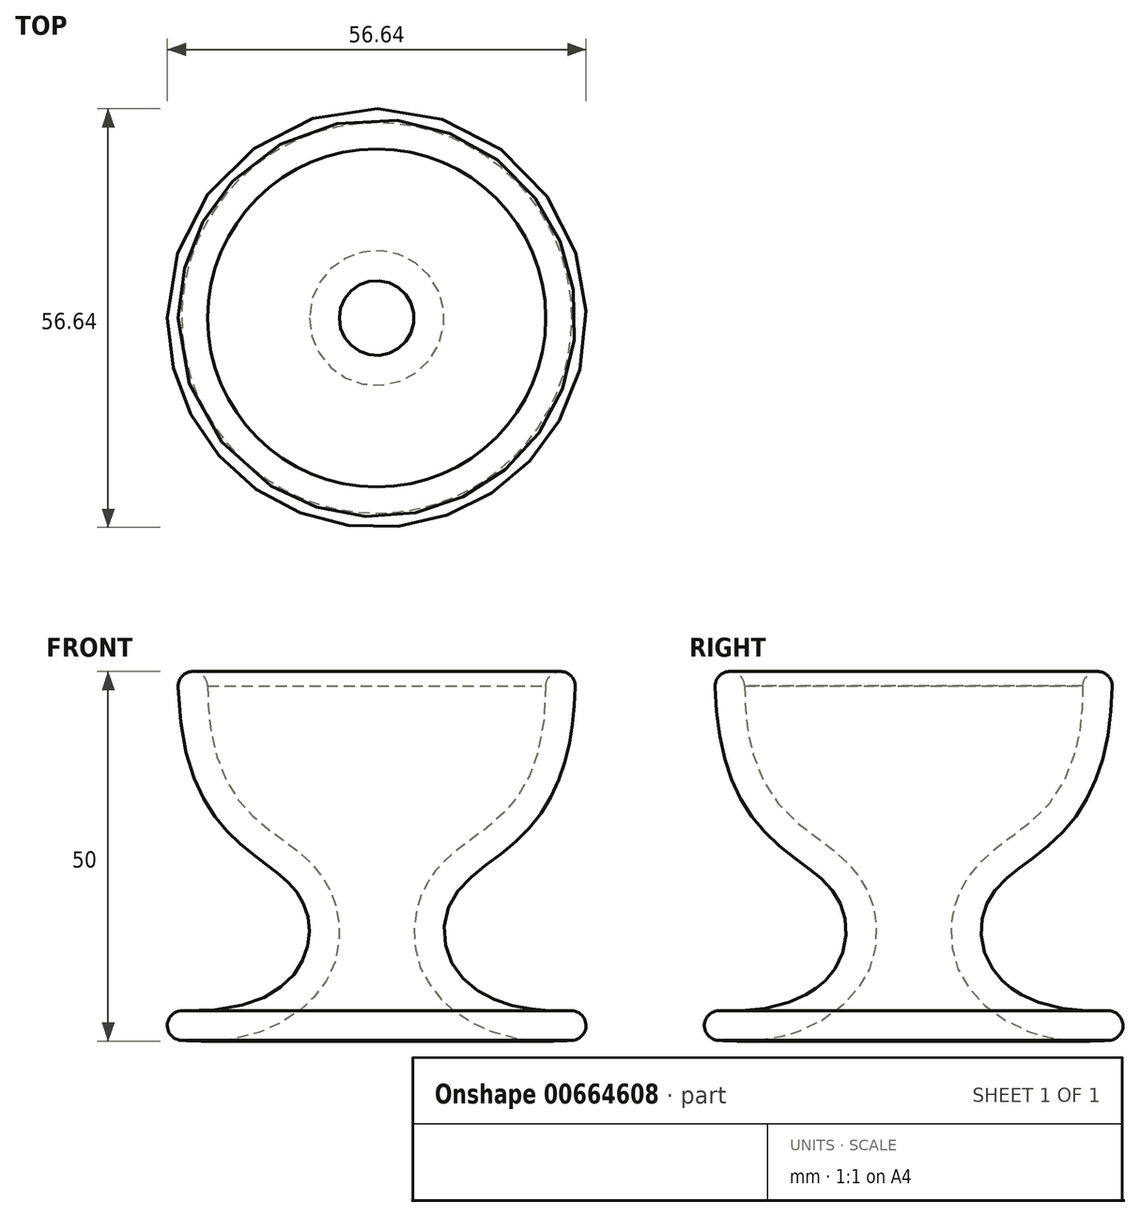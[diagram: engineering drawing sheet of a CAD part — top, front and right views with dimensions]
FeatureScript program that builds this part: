
annotation { "Feature Type Name" : "Feature", "Feature Type Description" : "" }
export const myFeature = defineFeature(function(context is Context, id is Id, definition is map)
    precondition{}
    {
        {
            var Q0;
            Q0=qCreatedBy(makeId("Front.planeOp"),FACE);
            var sketch = newSketch(context, id + "F0", { "sketchPlane" : qUnion([Q0])});
            skEllipticalArc(sketch, "E0", {"construction": true});
            skArc(sketch, "E1", {"start": v(21.5, 0) * mm, "mid": v(0, -21.5) * mm, "end": v(-21.5, 0) * mm, "construction": true});
            skFitSpline(sketch, "E2", {"points": [v(-26.87, 0) * mm, v(-10.16, -28.84) * mm, v(-26.24, -43.84) * mm], "startDerivative": vector(3.4, -120.3) * mm, "endDerivative": vector(-108.72, 4.18) * mm});
            skFitSpline(sketch, "E3.0", {"points": [v(-22.87, 0.11) * mm, v(-22.8, -2.22) * mm, v(-22.4, -6.28) * mm, v(-21.17, -10.8) * mm, v(-19.57, -14.07) * mm, v(-17.71, -16.52) * mm, v(-15.63, -18.5) * mm, v(-13.32, -20.26) * mm, v(-11.27, -21.77) * mm, v(-9.61, -23.18) * mm, v(-8.4, -24.4) * mm, v(-7.45, -25.59) * mm, v(-6.77, -26.67) * mm, v(-6.17, -27.84) * mm, v(-5.6, -29.37) * mm, v(-5.18, -31.31) * mm, v(-5.07, -33.34) * mm, v(-5.33, -36.09) * mm, v(-6.28, -38.85) * mm, v(-7.98, -41.4) * mm, v(-9.63, -43.14) * mm, v(-11.62, -44.65) * mm, v(-14.72, -46.3) * mm, v(-19.36, -47.67) * mm, v(-23.9, -47.93) * mm, v(-26.4, -47.84) * mm]});
            skArc(sketch, "E4", {"start": v(-22.87, 0.11) * mm, "mid": v(-24.92, 2.06) * mm, "end": v(-26.87, 0) * mm});
            skArc(sketch, "E5", {"start": v(-26.24, -43.84) * mm, "mid": v(-28.32, -45.76) * mm, "end": v(-26.4, -47.84) * mm});
            skLineSegment(sketch, "E6", {"start": v(0, -46.5) * mm, "end": v(0, -3.95) * mm});
            const initialGuessF0  = {"E0": [0, 0, 0, -1, 0.0315, 0.0215, 1.5707963267948966, 4.71238898038469]};
            skSetInitialGuess(sketch, initialGuessF0);
            skSolve(sketch);
        }
        {
            var Q0;
            Q0=makeQuery(id+"F0.imprint","IMPRINT",FACE,{"disambiguationData":[TD([[makeQuery(id+"F0.imprint","IMPRINT",EDGE,{"derivedFrom":sQuery(id+"F0.wireOp",EDGE,"E2")}),1.0]])]});
            var Q1;
            Q1=sQuery(id+"F0.wireOp",EDGE,"E6");
            revolve(context, id + "F1", {"entities" : qUnion([Q0]), "axis" : qUnion([Q1]), "revolveType" : RevolveType.FULL});
        }
    });
